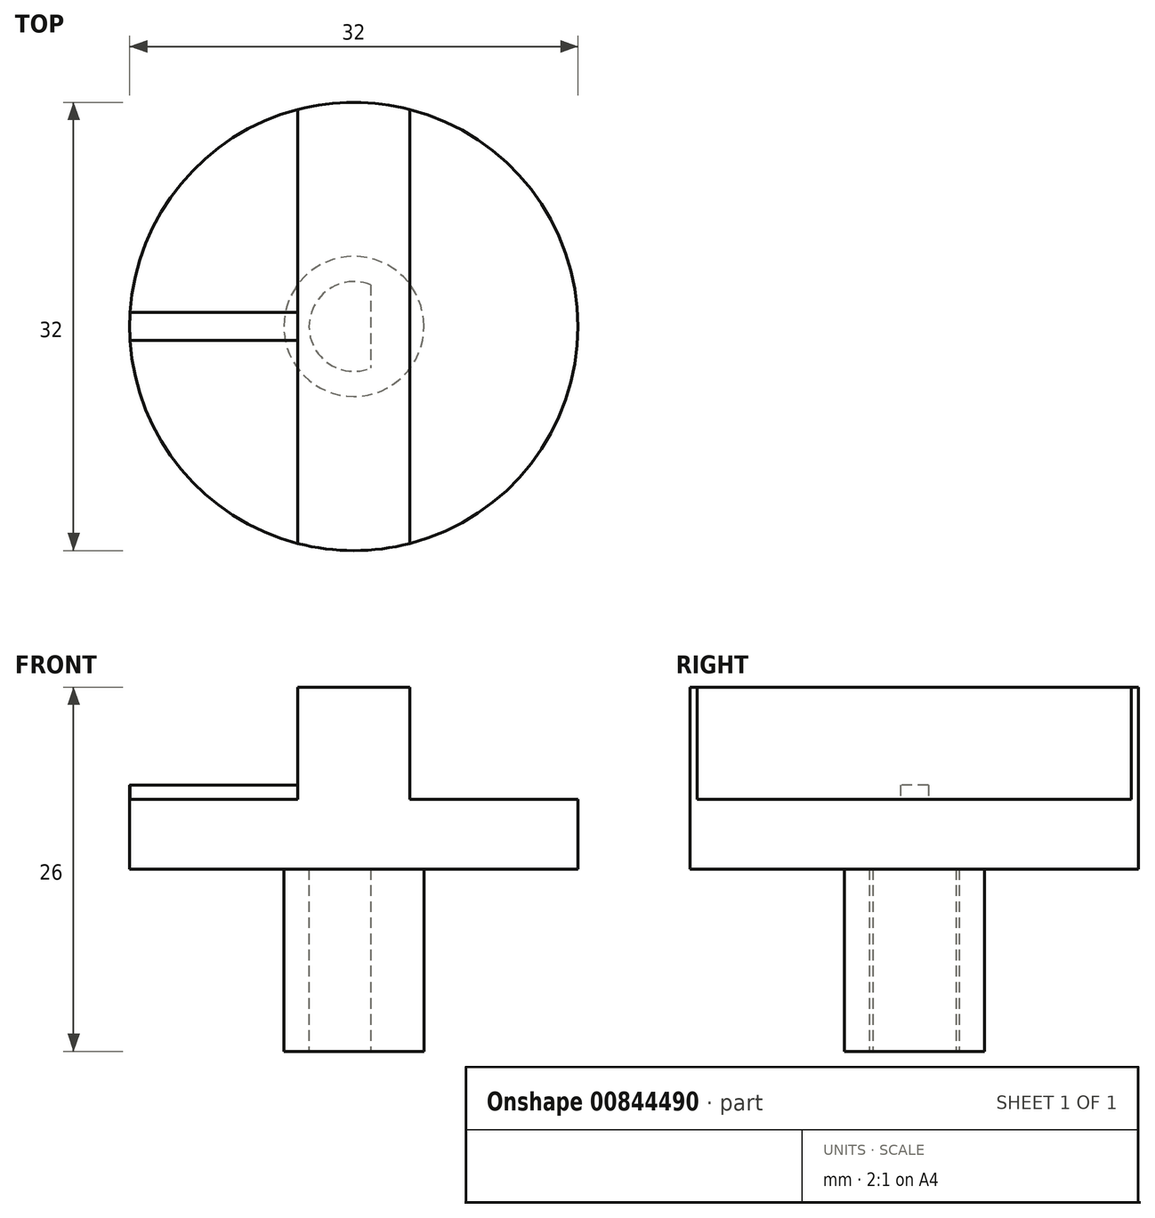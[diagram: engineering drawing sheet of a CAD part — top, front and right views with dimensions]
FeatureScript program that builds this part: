
annotation { "Feature Type Name" : "Feature", "Feature Type Description" : "" }
export const myFeature = defineFeature(function(context is Context, id is Id, definition is map)
    precondition{}
    {
        {
            var Q0;
            Q0=qCreatedBy(makeId("Top.planeOp"),FACE);
            var sketch = newSketch(context, id + "F0", { "sketchPlane" : qUnion([Q0])});
            skCircle(sketch, "E0", {"center": v(0, 0) * mm, "radius": 5 * mm});
            skArc(sketch, "E1", {"start": v(1.2, 2.97) * mm, "mid": v(-3.2, 0) * mm, "end": v(1.2, -2.97) * mm});
            skLineSegment(sketch, "E2", {"start": v(1.2, 2.97) * mm, "end": v(1.2, -2.97) * mm});
            skPoint(sketch, "E3", {"position": v(3.2, 0) * mm});
            skPoint(sketch, "E3.positionSnap0", {"position": v(1.2, 0) * mm});
            skSolve(sketch);
        }
        {
            var Q0;
            Q0 = qSketchRegion(id + "F0", true);
            extrude(context, id + "F1", {"entities" : qUnion([Q0]), "depth" : 13 * mm, "offsetDistance" : 25 * mm});
        }
        {
            var Q0;
            Q0=makeQuery(id+"F1.opExtrude","CAP_FACE",FACE,{"disambiguationData":[OSD([sQuery(id+"F0.wireOp",EDGE,"E0"),sQuery(id+"F0.wireOp",EDGE,"E1"),sQuery(id+"F0.wireOp",EDGE,"E2")])],"isStart":false});
            var sketch = newSketch(context, id + "F2", { "sketchPlane" : qUnion([Q0])});
            skCircle(sketch, "E4", {"center": v(0, 0) * mm, "radius": 16 * mm});
            skSolve(sketch);
        }
        {
            var Q0;
            Q0=makeQuery(id+"F2.imprint","IMPRINT",FACE,{"disambiguationData":[TD([[makeQuery(id+"F2.imprint","IMPRINT",EDGE,{"derivedFrom":sQuery(id+"F2.wireOp",EDGE,"E4")}),1.0]])]});
            var Q1;
            Q1=makeQuery(id+"F2.imprint","IMPRINT",FACE,{"disambiguationData":[TD([[makeQuery(id+"F2.imprint","IMPRINT",EDGE,{"derivedFrom":makeQuery(id+"F1.opExtrude","CAP_EDGE",EDGE,{"disambiguationData":[OSD([sQuery(id+"F0.wireOp",EDGE,"E0")])],"isStart":false})}),1.0]])]});
            var Q2;
            Q2=makeQuery(id+"F2.imprint","IMPRINT",FACE,{"disambiguationData":[TD([[makeQuery(id+"F2.imprint","IMPRINT",EDGE,{"derivedFrom":makeQuery(id+"F1.opExtrude","CAP_EDGE",EDGE,{"disambiguationData":[OSD([sQuery(id+"F0.wireOp",EDGE,"E1")])],"isStart":false})}),1.0]])]});
            extrude(context, id + "F3", {"entities" : qUnion([Q0, Q1, Q2]), "operationType" : NewBodyOperationType.ADD, "depth" : 5 * mm, "offsetDistance" : 25 * mm});
        }
        {
            var Q0;
            Q0=makeQuery(id+"F3.opExtrude","CAP_FACE",FACE,{"disambiguationData":[OSD([sQuery(id+"F2.wireOp",EDGE,"E4")])],"isStart":false});
            var sketch = newSketch(context, id + "F4", { "sketchPlane" : qUnion([Q0])});
            skLineSegment(sketch, "E5", {"start": v(0, 17.7) * mm, "end": v(0, -17.48) * mm, "construction": true});
            skPoint(sketch, "E6", {"position": v(-4, 15.5) * mm});
            skPoint(sketch, "E7", {"position": v(4, 15.5) * mm});
            skPoint(sketch, "E8", {"position": v(-4, -15.5) * mm});
            skPoint(sketch, "E9", {"position": v(4, -15.5) * mm});
            skLineSegment(sketch, "E10", {"start": v(-4, 15.5) * mm, "end": v(-4, -15.5) * mm});
            skLineSegment(sketch, "E11", {"start": v(4, 15.5) * mm, "end": v(4, -15.5) * mm});
            skSolve(sketch);
        }
        {
            var Q0;
            Q0 = qSketchRegion(id + "F4", true);
            var Q1;
            {var subQ0=sQuery(id+"F4.wireOp",EDGE,"E10");Q1=makeQuery(id+"F4.imprint","IMPRINT",FACE,{"disambiguationData":[TD([[makeQuery(id+"F4.imprint","IMPRINT",EDGE,{"derivedFrom":subQ0}),1.0]])]});}
            extrude(context, id + "F5", {"entities" : qUnion([Q0, Q1]), "operationType" : NewBodyOperationType.ADD, "depth" : 8 * mm, "offsetDistance" : 25 * mm});
        }
        {
            var Q0;
            {var subQ0=sQuery(id+"F2.wireOp",EDGE,"E4");var subQ1=sQuery(id+"F4.wireOp",EDGE,"E10");Q0=makeQuery(id+"F5.boolean.opBoolean","SPLIT",FACE,{"disambiguationData":[TD([makeQuery(id+"F5.opExtrude","SWEPT_FACE",FACE,{"disambiguationData":[OSD([subQ1])]})])],"derivedFrom":makeQuery(id+"F3.opExtrude","CAP_FACE",FACE,{"disambiguationData":[OSD([subQ0])],"isStart":false})});}
            var sketch = newSketch(context, id + "F6", { "sketchPlane" : qUnion([Q0])});
            skPoint(sketch, "E12", {"position": v(-15.97, 1) * mm});
            skPoint(sketch, "E13", {"position": v(-15.97, -1) * mm});
            skPoint(sketch, "E14", {"position": v(-4, -1) * mm});
            skPoint(sketch, "E15", {"position": v(-4, 1) * mm});
            skLineSegment(sketch, "E16", {"start": v(6.27, 0) * mm, "end": v(-22.09, 0) * mm, "construction": true});
            skLineSegment(sketch, "E17", {"start": v(-15.97, 1) * mm, "end": v(-4, 1) * mm});
            skLineSegment(sketch, "E18", {"start": v(-4, -1) * mm, "end": v(-15.97, -1) * mm});
            skSolve(sketch);
        }
        {
            var Q0;
            Q0 = qSketchRegion(id + "F6", true);
            var Q1;
            {var subQ0=sQuery(id+"F6.wireOp",EDGE,"E17");Q1=makeQuery(id+"F6.imprint","IMPRINT",FACE,{"disambiguationData":[TD([[makeQuery(id+"F6.imprint","IMPRINT",EDGE,{"derivedFrom":subQ0}),-1.0]])]});}
            extrude(context, id + "F7", {"entities" : qUnion([Q0, Q1]), "operationType" : NewBodyOperationType.ADD, "depth" : 1 * mm, "offsetDistance" : 25 * mm});
        }
    });
